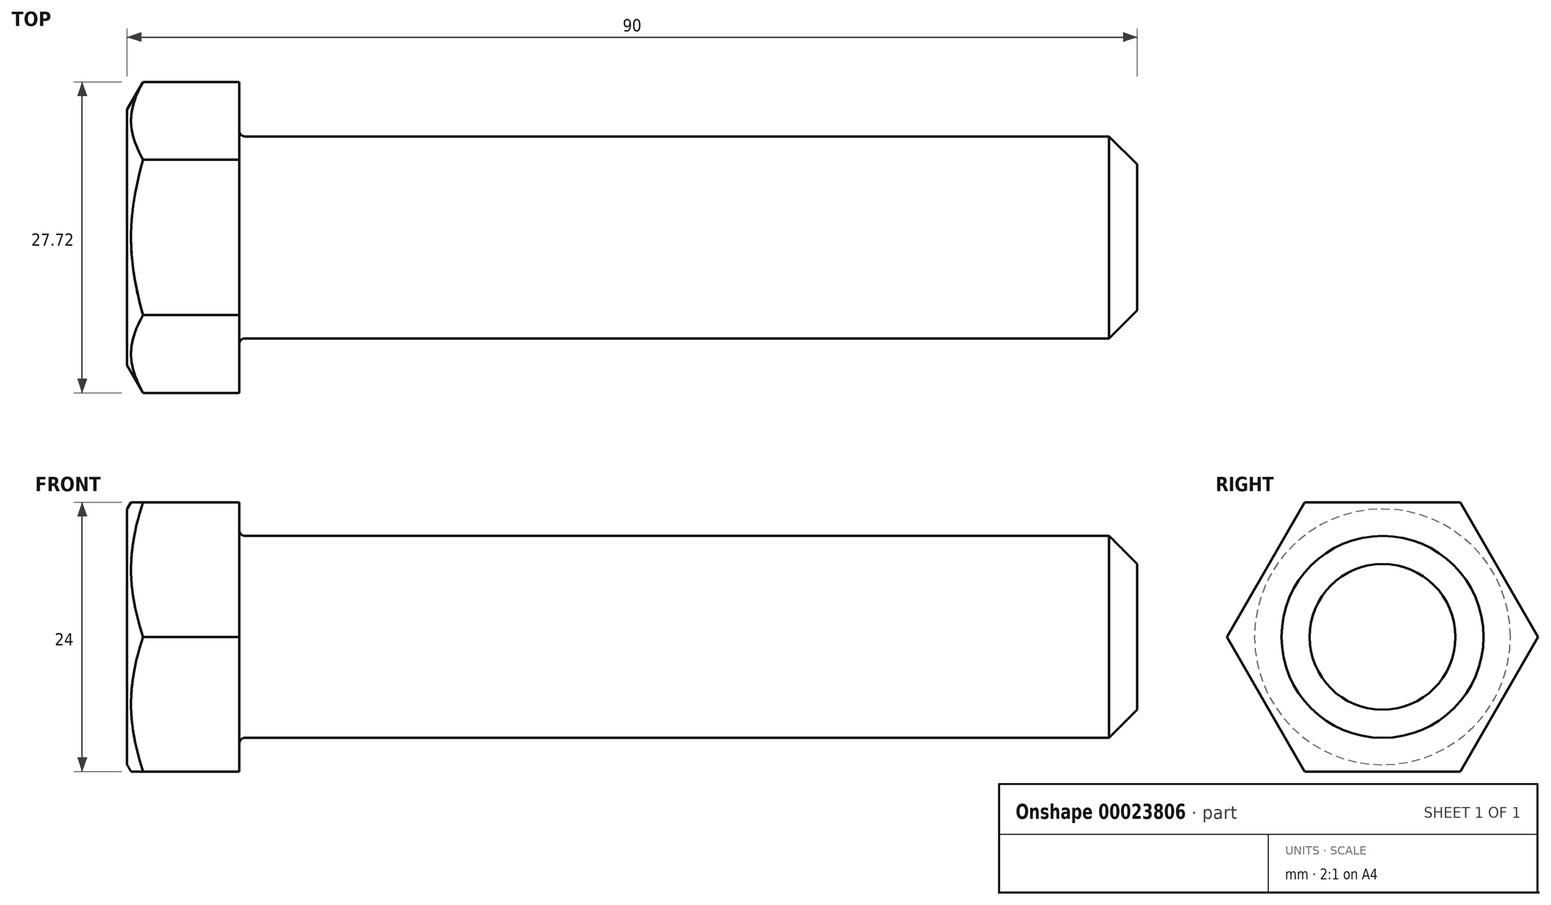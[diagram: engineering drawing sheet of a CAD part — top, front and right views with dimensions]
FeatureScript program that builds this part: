
annotation { "Feature Type Name" : "Feature", "Feature Type Description" : "" }
export const myFeature = defineFeature(function(context is Context, id is Id, definition is map)
    precondition{}
    {
        {
            var Q0;
            Q0=qCreatedBy(makeId("Front.planeOp"),FACE);
            var sketch = newSketch(context, id + "F0", { "sketchPlane" : qUnion([Q0])});
            skLineSegment(sketch, "E0", {"start": v(0, 0) * mm, "end": v(0, 11.4) * mm});
            skLineSegment(sketch, "E1", {"start": v(0, 11.4) * mm, "end": v(10, 28.72) * mm});
            skLineSegment(sketch, "E2", {"start": v(10, 28.72) * mm, "end": v(10, 9) * mm});
            skLineSegment(sketch, "E3", {"start": v(10, 9) * mm, "end": v(90, 9) * mm});
            skLineSegment(sketch, "E4", {"start": v(90, 9) * mm, "end": v(90, 0) * mm});
            skLineSegment(sketch, "E5", {"start": v(90, 0) * mm, "end": v(0, 0) * mm});
            skSolve(sketch);
        }
        {
            var Q0;
            Q0 = qSketchRegion(id + "F0", true);
            var Q1;
            Q1=sQuery(id+"F0.wireOp",EDGE,"E5");
            revolve(context, id + "F1", {"entities" : qUnion([Q0]), "axis" : qUnion([Q1]), "revolveType" : RevolveType.FULL});
        }
        {
            var Q0;
            Q0=makeQuery(id+"F1.opRevolve","SWEPT_FACE",FACE,{"disambiguationData":[OSD([sQuery(id+"F0.wireOp",EDGE,"E2")])]});
            var sketch = newSketch(context, id + "F2", { "sketchPlane" : qUnion([Q0])});
            skCircle(sketch, "E6.cCircle", {"center": v(0, 0) * mm, "radius": 12 * mm, "construction": true});
            skLineSegment(sketch, "E6.0", {"start": v(-6.93, 12) * mm, "end": v(6.93, 12) * mm});
            skLineSegment(sketch, "E6.1", {"start": v(6.93, 12) * mm, "end": v(13.86, 0) * mm});
            skLineSegment(sketch, "E6.2", {"start": v(13.86, 0) * mm, "end": v(6.93, -12) * mm});
            skLineSegment(sketch, "E6.3", {"start": v(6.93, -12) * mm, "end": v(-6.93, -12) * mm});
            skLineSegment(sketch, "E6.4", {"start": v(-6.93, -12) * mm, "end": v(-13.86, 0) * mm});
            skLineSegment(sketch, "E6.5", {"start": v(-13.86, 0) * mm, "end": v(-6.93, 12) * mm});
            skPoint(sketch, "E6.0.midPoint", {"position": v(0, 12) * mm});
            skCircle(sketch, "E7.0", {"center": v(0, 0) * mm, "radius": 28.72 * mm});
            skSolve(sketch);
        }
        {
            var Q0;
            Q0 = qSketchRegion(id + "F2", true);
            extrude(context, id + "F3", {"entities" : qUnion([Q0]), "operationType" : NewBodyOperationType.REMOVE, "endBound" : BoundingType.THROUGH_ALL, "oppositeDirection" : true, "depth" : 25 * mm});
        }
        {
            var Q0;
            Q0=makeQuery(id+"F1.opRevolve","SWEPT_EDGE",EDGE,{"disambiguationData":[OSD([sQuery(id+"F0.wireOp",EDGE,"E2"),sQuery(id+"F0.wireOp",EDGE,"E3")])]});
            fillet(context, id + "F4", {"entities" : qUnion([Q0]), "radius" : .5 * mm, "tangentPropagation" : true, "allowEdgeOverflow" : false});
        }
        {
            var Q0;
            Q0=makeQuery(id+"F1.opRevolve","SWEPT_EDGE",EDGE,{"disambiguationData":[OSD([sQuery(id+"F0.wireOp",EDGE,"E3"),sQuery(id+"F0.wireOp",EDGE,"E4")])]});
            chamfer(context, id + "F5", {"entities" : qUnion([Q0]), "width" : 2.5 * mm, "tangentPropagation" : true});
        }
    });
